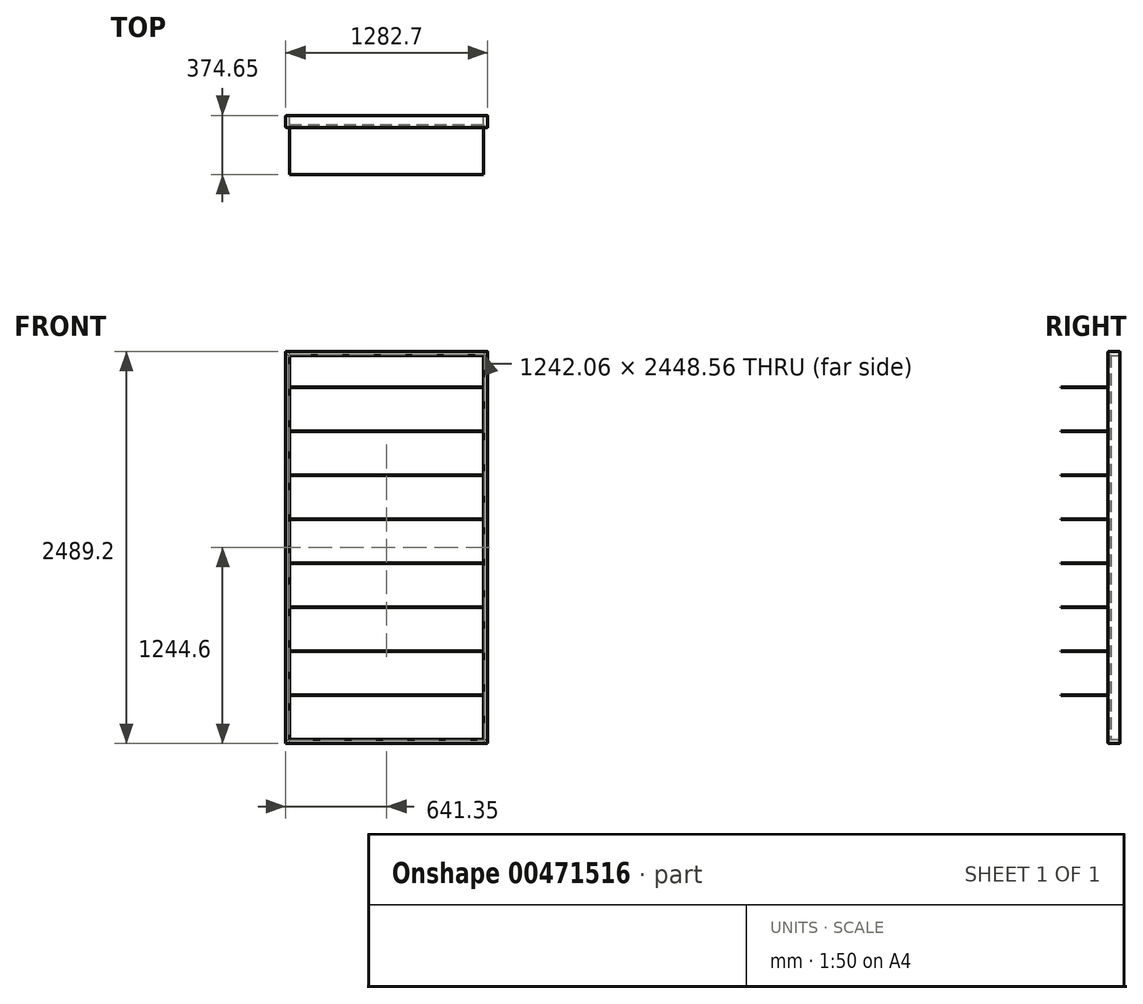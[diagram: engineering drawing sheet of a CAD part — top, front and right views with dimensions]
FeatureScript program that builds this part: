
annotation { "Feature Type Name" : "Feature", "Feature Type Description" : "" }
export const myFeature = defineFeature(function(context is Context, id is Id, definition is map)
    precondition{}
    {
        {
            var Q0;
            Q0=qCreatedBy(makeId("Front.planeOp"),FACE);
            var sketch = newSketch(context, id + "F0", { "sketchPlane" : qUnion([Q0])});
            skLineSegment(sketch, "E0.bottom", {"start": v(0, 0) * mm, "end": v(1282.7, 0) * mm});
            skLineSegment(sketch, "E0.top", {"start": v(0, 2489.2) * mm, "end": v(1282.7, 2489.2) * mm});
            skLineSegment(sketch, "E0.left", {"start": v(0, 0) * mm, "end": v(0, 2489.2) * mm});
            skLineSegment(sketch, "E0.right", {"start": v(1282.7, 0) * mm, "end": v(1282.7, 2489.2) * mm});
            skLineSegment(sketch, "E1.0", {"start": v(25.4, 2463.8) * mm, "end": v(1257.3, 2463.8) * mm});
            skLineSegment(sketch, "E1.1", {"start": v(25.4, 25.4) * mm, "end": v(25.4, 2463.8) * mm});
            skLineSegment(sketch, "E1.2", {"start": v(25.4, 25.4) * mm, "end": v(1257.3, 25.4) * mm});
            skLineSegment(sketch, "E1.3", {"start": v(1257.3, 25.4) * mm, "end": v(1257.3, 2463.8) * mm});
            skSolve(sketch);
        }
        {
            var Q0;
            Q0 = qSketchRegion(id + "F0", true);
            extrude(context, id + "F1", {"entities" : qUnion([Q0]), "depth" : 76.2 * mm});
        }
        {
            var Q0;
            Q0=makeQuery(id+"F1.opExtrude","CAP_FACE",FACE,{"disambiguationData":[OSD([sQuery(id+"F0.wireOp",EDGE,"E0.bottom"),sQuery(id+"F0.wireOp",EDGE,"E0.top"),sQuery(id+"F0.wireOp",EDGE,"E0.left"),sQuery(id+"F0.wireOp",EDGE,"E0.right"),sQuery(id+"F0.wireOp",EDGE,"E1.0"),sQuery(id+"F0.wireOp",EDGE,"E1.1"),sQuery(id+"F0.wireOp",EDGE,"E1.2"),sQuery(id+"F0.wireOp",EDGE,"E1.3")])],"isStart":false});
            var Q1;
            Q1=makeQuery(id+"F1.opExtrude","CAP_FACE",FACE,{"disambiguationData":[OSD([sQuery(id+"F0.wireOp",EDGE,"E0.bottom"),sQuery(id+"F0.wireOp",EDGE,"E0.top"),sQuery(id+"F0.wireOp",EDGE,"E0.left"),sQuery(id+"F0.wireOp",EDGE,"E0.right"),sQuery(id+"F0.wireOp",EDGE,"E1.0"),sQuery(id+"F0.wireOp",EDGE,"E1.1"),sQuery(id+"F0.wireOp",EDGE,"E1.2"),sQuery(id+"F0.wireOp",EDGE,"E1.3")])],"isStart":true});
            fillet(context, id + "F2", {"entities" : qUnion([Q0, Q1]), "radius" : 5.08 * mm, "tangentPropagation" : true, "allowEdgeOverflow" : false});
        }
        {
            var Q0;
            Q0=makeQuery(id+"F1.opExtrude","CAP_FACE",FACE,{"disambiguationData":[OSD([sQuery(id+"F0.wireOp",EDGE,"E0.bottom"),sQuery(id+"F0.wireOp",EDGE,"E0.top"),sQuery(id+"F0.wireOp",EDGE,"E0.left"),sQuery(id+"F0.wireOp",EDGE,"E0.right"),sQuery(id+"F0.wireOp",EDGE,"E1.0"),sQuery(id+"F0.wireOp",EDGE,"E1.1"),sQuery(id+"F0.wireOp",EDGE,"E1.2"),sQuery(id+"F0.wireOp",EDGE,"E1.3")])],"isStart":false});
            cPlane(context, id + "F3", {"entities" : qUnion([Q0]), "cplaneType" : CPlaneType.OFFSET, "offset" : 6.35 * mm, "oppositeDirection" : true, "width" : 152.4 * mm, "height" : 152.4 * mm});
        }
        {
            var Q0;
            Q0=qCreatedBy(id+"F3.planeOp",FACE);
            var sketch = newSketch(context, id + "F4", { "sketchPlane" : qUnion([Q0])});
            skLineSegment(sketch, "E2.bottom", {"start": v(25.4, 2463.8) * mm, "end": v(1257.3, 2463.8) * mm});
            skLineSegment(sketch, "E2.top", {"start": v(25.4, 25.4) * mm, "end": v(1257.3, 25.4) * mm});
            skLineSegment(sketch, "E2.left", {"start": v(25.4, 2463.8) * mm, "end": v(25.4, 25.4) * mm});
            skLineSegment(sketch, "E2.right", {"start": v(1257.3, 2463.8) * mm, "end": v(1257.3, 25.4) * mm});
            skSolve(sketch);
        }
        {
            var Q0;
            Q0 = qSketchRegion(id + "F4", true);
            extrude(context, id + "F5", {"entities" : qUnion([Q0]), "oppositeDirection" : true, "depth" : 12.7 * mm});
        }
        {
            var Q0;
            Q0=makeQuery(id+"F5.opExtrude","CAP_FACE",FACE,{"disambiguationData":[OSD([sQuery(id+"F4.wireOp",EDGE,"E2.bottom"),sQuery(id+"F4.wireOp",EDGE,"E2.top"),sQuery(id+"F4.wireOp",EDGE,"E2.left"),sQuery(id+"F4.wireOp",EDGE,"E2.right")])],"isStart":true});
            var sketch = newSketch(context, id + "F6", { "sketchPlane" : qUnion([Q0])});
            skLineSegment(sketch, "E3.bottom", {"start": v(25.4, 307.97) * mm, "end": v(1257.3, 307.97) * mm});
            skLineSegment(sketch, "E3.top", {"start": v(25.4, 304.8) * mm, "end": v(1257.3, 304.8) * mm});
            skLineSegment(sketch, "E3.left", {"start": v(25.4, 307.97) * mm, "end": v(25.4, 304.8) * mm});
            skLineSegment(sketch, "E3.right", {"start": v(1257.3, 307.97) * mm, "end": v(1257.3, 304.8) * mm});
            skLineSegment(sketch, "E4.0.1.0", {"start": v(25.4, 587.38) * mm, "end": v(1257.3, 587.38) * mm});
            skLineSegment(sketch, "E4.0.1.1", {"start": v(25.4, 584.2) * mm, "end": v(1257.3, 584.2) * mm});
            skLineSegment(sketch, "E4.0.1.2", {"start": v(25.4, 587.38) * mm, "end": v(25.4, 584.2) * mm});
            skLineSegment(sketch, "E4.0.1.3", {"start": v(1257.3, 587.38) * mm, "end": v(1257.3, 584.2) * mm});
            skLineSegment(sketch, "E4.0.2.0", {"start": v(25.4, 866.78) * mm, "end": v(1257.3, 866.78) * mm});
            skLineSegment(sketch, "E4.0.2.1", {"start": v(25.4, 863.6) * mm, "end": v(1257.3, 863.6) * mm});
            skLineSegment(sketch, "E4.0.2.2", {"start": v(25.4, 866.78) * mm, "end": v(25.4, 863.6) * mm});
            skLineSegment(sketch, "E4.0.2.3", {"start": v(1257.3, 866.78) * mm, "end": v(1257.3, 863.6) * mm});
            skLineSegment(sketch, "E4.0.3.0", {"start": v(25.4, 1146.18) * mm, "end": v(1257.3, 1146.18) * mm});
            skLineSegment(sketch, "E4.0.3.1", {"start": v(25.4, 1143) * mm, "end": v(1257.3, 1143) * mm});
            skLineSegment(sketch, "E4.0.3.2", {"start": v(25.4, 1146.18) * mm, "end": v(25.4, 1143) * mm});
            skLineSegment(sketch, "E4.0.3.3", {"start": v(1257.3, 1146.18) * mm, "end": v(1257.3, 1143) * mm});
            skLineSegment(sketch, "E4.0.4.0", {"start": v(25.4, 1425.58) * mm, "end": v(1257.3, 1425.58) * mm});
            skLineSegment(sketch, "E4.0.4.1", {"start": v(25.4, 1422.4) * mm, "end": v(1257.3, 1422.4) * mm});
            skLineSegment(sketch, "E4.0.4.2", {"start": v(25.4, 1425.58) * mm, "end": v(25.4, 1422.4) * mm});
            skLineSegment(sketch, "E4.0.4.3", {"start": v(1257.3, 1425.58) * mm, "end": v(1257.3, 1422.4) * mm});
            skLineSegment(sketch, "E4.0.5.0", {"start": v(25.4, 1704.98) * mm, "end": v(1257.3, 1704.98) * mm});
            skLineSegment(sketch, "E4.0.5.1", {"start": v(25.4, 1701.8) * mm, "end": v(1257.3, 1701.8) * mm});
            skLineSegment(sketch, "E4.0.5.2", {"start": v(25.4, 1704.98) * mm, "end": v(25.4, 1701.8) * mm});
            skLineSegment(sketch, "E4.0.5.3", {"start": v(1257.3, 1704.98) * mm, "end": v(1257.3, 1701.8) * mm});
            skLineSegment(sketch, "E4.0.6.0", {"start": v(25.4, 1984.38) * mm, "end": v(1257.3, 1984.38) * mm});
            skLineSegment(sketch, "E4.0.6.1", {"start": v(25.4, 1981.2) * mm, "end": v(1257.3, 1981.2) * mm});
            skLineSegment(sketch, "E4.0.6.2", {"start": v(25.4, 1984.38) * mm, "end": v(25.4, 1981.2) * mm});
            skLineSegment(sketch, "E4.0.6.3", {"start": v(1257.3, 1984.38) * mm, "end": v(1257.3, 1981.2) * mm});
            skLineSegment(sketch, "E4.0.7.0", {"start": v(25.4, 2263.78) * mm, "end": v(1257.3, 2263.78) * mm});
            skLineSegment(sketch, "E4.0.7.1", {"start": v(25.4, 2260.6) * mm, "end": v(1257.3, 2260.6) * mm});
            skLineSegment(sketch, "E4.0.7.2", {"start": v(25.4, 2263.78) * mm, "end": v(25.4, 2260.6) * mm});
            skLineSegment(sketch, "E4.0.7.3", {"start": v(1257.3, 2263.78) * mm, "end": v(1257.3, 2260.6) * mm});
            skLineSegment(sketch, "E4.direction1", {"start": v(25.4, 307.97) * mm, "end": v(50.8, 307.97) * mm, "construction": true});
            skLineSegment(sketch, "E4.direction2", {"start": v(25.4, 307.97) * mm, "end": v(25.4, 587.38) * mm, "construction": true});
            skSolve(sketch);
        }
        {
            var Q0;
            Q0 = qSketchRegion(id + "F6", true);
            extrude(context, id + "F7", {"entities" : qUnion([Q0]), "depth" : 304.8 * mm});
        }
    });
